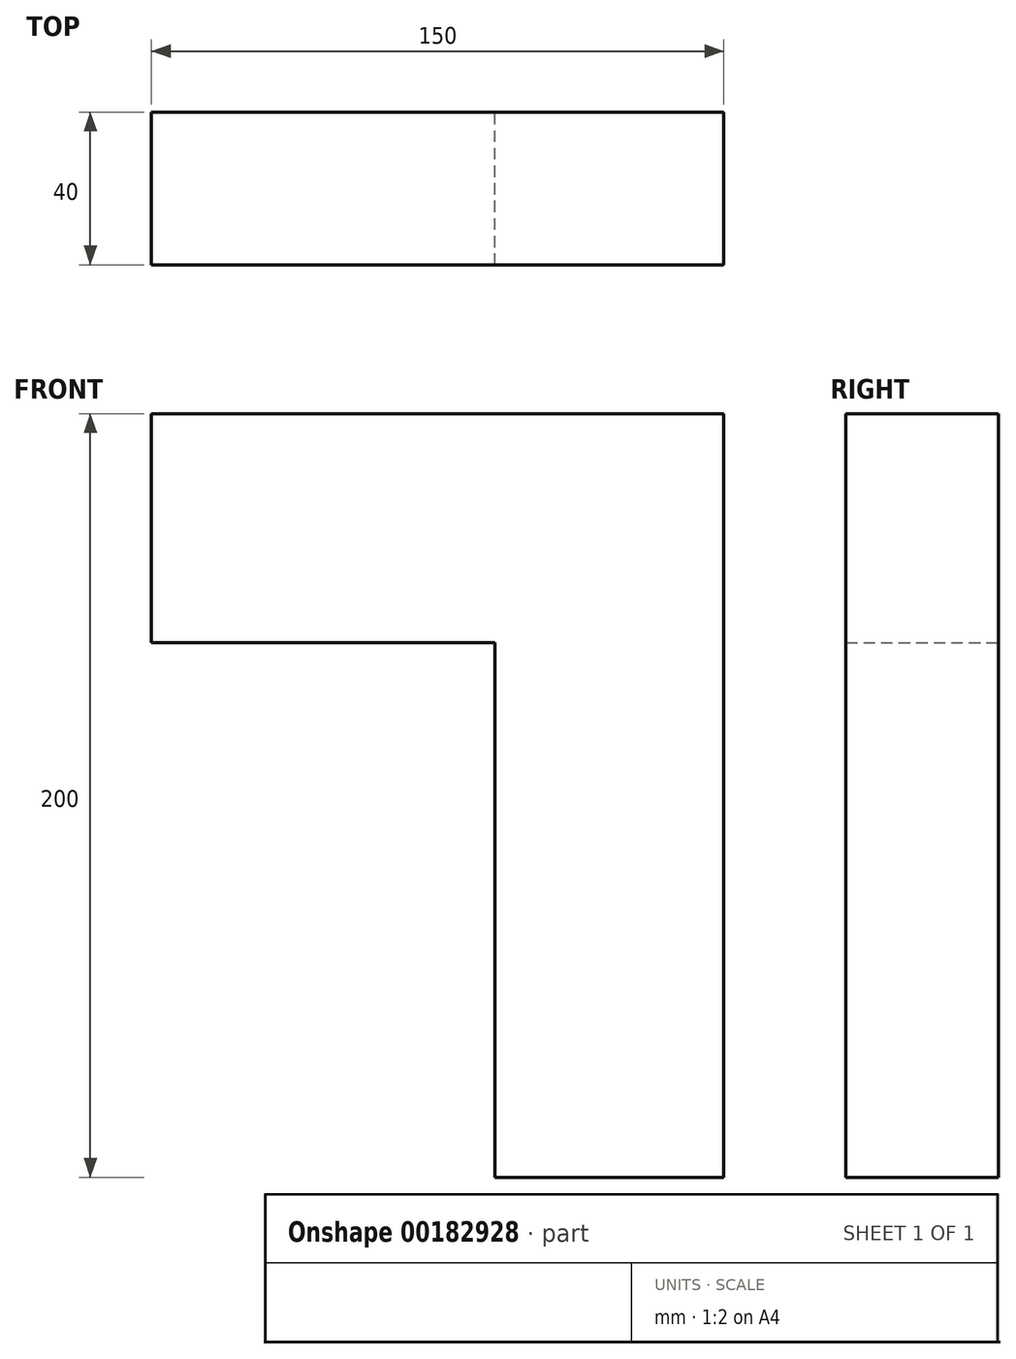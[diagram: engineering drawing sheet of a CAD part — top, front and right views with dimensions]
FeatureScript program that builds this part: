
annotation { "Feature Type Name" : "Feature", "Feature Type Description" : "" }
export const myFeature = defineFeature(function(context is Context, id is Id, definition is map)
    precondition{}
    {
        {
            var Q0;
            Q0=qCreatedBy(makeId("Front.planeOp"),FACE);
            var sketch = newSketch(context, id + "F0", { "sketchPlane" : qUnion([Q0])});
            skLineSegment(sketch, "E0", {"start": v(0, 0) * mm, "end": v(0, 200) * mm});
            skLineSegment(sketch, "E1", {"start": v(-150, 200) * mm, "end": v(-150, 140) * mm});
            skLineSegment(sketch, "E2", {"start": v(-150, 140) * mm, "end": v(-60, 140) * mm});
            skLineSegment(sketch, "E3", {"start": v(-60, 140) * mm, "end": v(-60, 0) * mm});
            skLineSegment(sketch, "E4", {"start": v(-60, 0) * mm, "end": v(0, 0) * mm});
            skLineSegment(sketch, "E5", {"start": v(0, 200) * mm, "end": v(-150, 200) * mm});
            skSolve(sketch);
        }
        {
            var Q0;
            Q0 = qSketchRegion(id + "F0", true);
            extrude(context, id + "F1", {"entities" : qUnion([Q0]), "depth" : 40 * mm});
        }
    });
